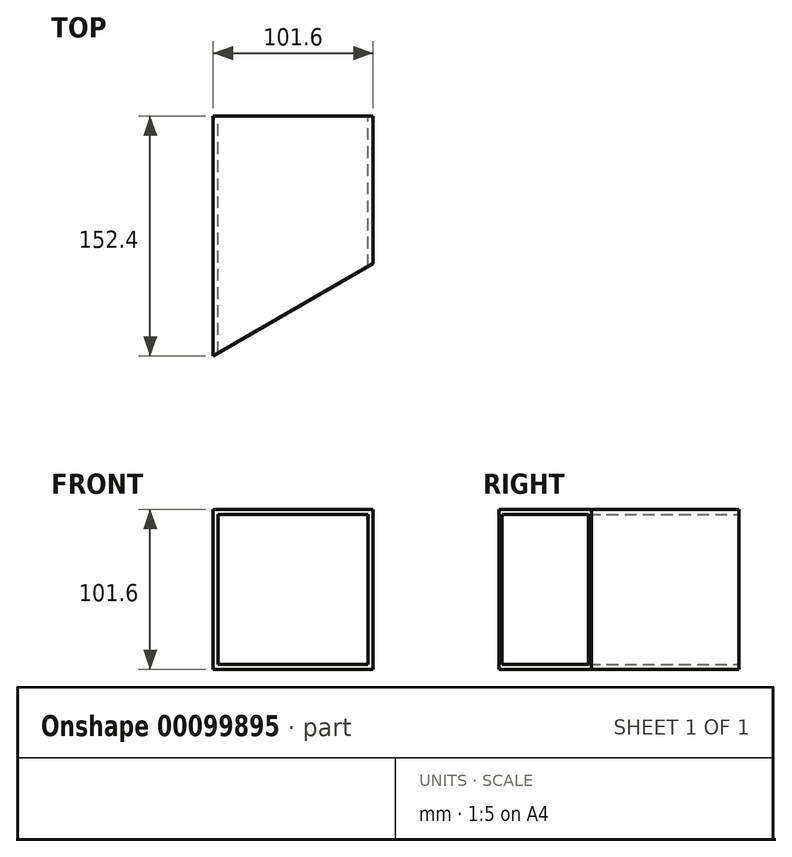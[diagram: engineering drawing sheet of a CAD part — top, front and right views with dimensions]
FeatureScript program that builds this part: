
annotation { "Feature Type Name" : "Feature", "Feature Type Description" : "" }
export const myFeature = defineFeature(function(context is Context, id is Id, definition is map)
    precondition{}
    {
        {
            var Q0;
            Q0=qCreatedBy(makeId("Front.planeOp"),FACE);
            var sketch = newSketch(context, id + "F0", { "sketchPlane" : qUnion([Q0])});
            skLineSegment(sketch, "E0.bottom", {"start": v(50.8, 50.8) * mm, "end": v(-50.8, 50.8) * mm});
            skLineSegment(sketch, "E0.top", {"start": v(50.8, -50.8) * mm, "end": v(-50.8, -50.8) * mm});
            skLineSegment(sketch, "E0.left", {"start": v(50.8, 50.8) * mm, "end": v(50.8, -50.8) * mm});
            skLineSegment(sketch, "E0.right", {"start": v(-50.8, 50.8) * mm, "end": v(-50.8, -50.8) * mm});
            skPoint(sketch, "E0.middle", {"position": v(0, 0) * mm});
            skLineSegment(sketch, "E1.bottom", {"start": v(47.63, 47.62) * mm, "end": v(-47.63, 47.62) * mm});
            skLineSegment(sketch, "E1.top", {"start": v(47.63, -47.62) * mm, "end": v(-47.63, -47.62) * mm});
            skLineSegment(sketch, "E1.left", {"start": v(47.62, 47.62) * mm, "end": v(47.62, -47.62) * mm});
            skLineSegment(sketch, "E1.right", {"start": v(-47.62, 47.62) * mm, "end": v(-47.62, -47.62) * mm});
            skSolve(sketch);
        }
        {
            var Q0;
            Q0 = qSketchRegion(id + "F0", true);
            extrude(context, id + "F1", {"entities" : qUnion([Q0]), "depth" : 152.4 * mm});
        }
        {
            var Q0;
            Q0=qCreatedBy(makeId("Top.planeOp"),FACE);
            var sketch = newSketch(context, id + "F2", { "sketchPlane" : qUnion([Q0])});
            skLineSegment(sketch, "E2", {"start": v(50.8, -152.4) * mm, "end": v(-50.8, -152.4) * mm});
            skLineSegment(sketch, "E3", {"start": v(-50.8, -152.4) * mm, "end": v(50.8, -93.74) * mm});
            skLineSegment(sketch, "E4", {"start": v(50.8, -93.74) * mm, "end": v(50.8, -152.4) * mm});
            skSolve(sketch);
        }
        {
            var Q0;
            Q0 = qSketchRegion(id + "F2", true);
            extrude(context, id + "F3", {"entities" : qUnion([Q0]), "operationType" : NewBodyOperationType.REMOVE, "endBound" : BoundingType.THROUGH_ALL, "oppositeDirection" : true, "depth" : 25.4 * mm, "hasSecondDirection" : true, "secondDirectionBound" : BoundingType.THROUGH_ALL, "secondDirectionOppositeDirection" : false, "secondDirectionDepth" : 25.4 * mm});
        }
    });
